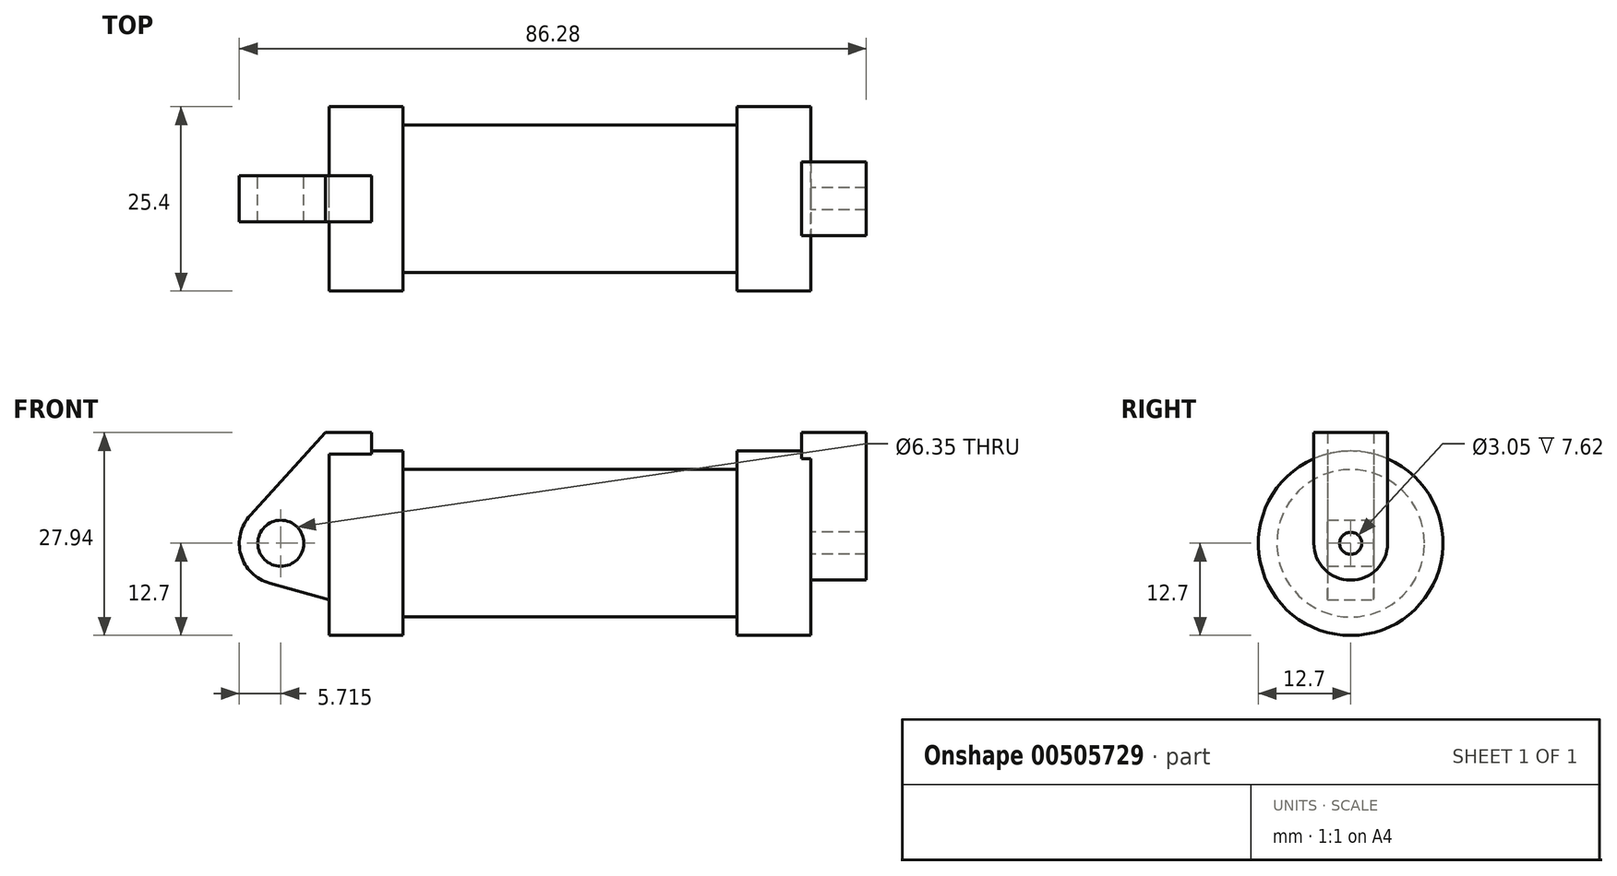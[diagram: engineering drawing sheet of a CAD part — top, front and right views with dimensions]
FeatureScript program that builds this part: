
annotation { "Feature Type Name" : "Feature", "Feature Type Description" : "" }
export const myFeature = defineFeature(function(context is Context, id is Id, definition is map)
    precondition{}
    {
        {
            var Q0;
            Q0=qCreatedBy(makeId("Front.planeOp"),FACE);
            var sketch = newSketch(context, id + "F0", { "sketchPlane" : qUnion([Q0])});
            skLineSegment(sketch, "E0", {"start": v(0, 0) * mm, "end": v(0, 12.7) * mm});
            skLineSegment(sketch, "E1", {"start": v(0, 12.7) * mm, "end": v(10.16, 12.7) * mm});
            skLineSegment(sketch, "E2", {"start": v(10.16, 12.7) * mm, "end": v(10.16, 10.16) * mm});
            skLineSegment(sketch, "E3", {"start": v(10.16, 10.16) * mm, "end": v(56.13, 10.16) * mm});
            skLineSegment(sketch, "E4", {"start": v(56.13, 10.16) * mm, "end": v(56.13, 12.7) * mm});
            skLineSegment(sketch, "E5", {"start": v(56.13, 12.7) * mm, "end": v(66.3, 12.7) * mm});
            skLineSegment(sketch, "E6", {"start": v(66.3, 12.7) * mm, "end": v(66.3, 0) * mm});
            skLineSegment(sketch, "E7", {"start": v(66.3, 0) * mm, "end": v(0, 0) * mm});
            skLineSegment(sketch, "E8", {"start": v(5.84, 15.24) * mm, "end": v(-0.5, 15.24) * mm});
            skLineSegment(sketch, "E9", {"start": v(-0.5, 15.24) * mm, "end": v(-10.88, 3.85) * mm});
            skLineSegment(sketch, "E10", {"start": v(0, 0) * mm, "end": v(-6.65, 0) * mm});
            skCircle(sketch, "E11", {"center": v(-6.65, 0) * mm, "radius": 5.72 * mm});
            skCircle(sketch, "E12", {"center": v(-6.65, 0) * mm, "radius": 3.18 * mm});
            skLineSegment(sketch, "E13", {"start": v(5.84, 15.24) * mm, "end": v(5.84, -9.4) * mm});
            skLineSegment(sketch, "E14", {"start": v(5.84, -9.4) * mm, "end": v(-8.18, -5.5) * mm});
            skSolve(sketch);
        }
        {
            var Q0;
            {var subQ0=sQuery(id+"F0.wireOp",EDGE,"E2");Q0=makeQuery(id+"F0.imprint","IMPRINT",FACE,{"disambiguationData":[TD([[makeQuery(id+"F0.imprint","IMPRINT",EDGE,{"derivedFrom":subQ0}),-1.0]])]});}
            var Q1;
            {var subQ0=sQuery(id+"F0.wireOp",EDGE,"E0");Q1=makeQuery(id+"F0.imprint","IMPRINT",FACE,{"disambiguationData":[TD([[makeQuery(id+"F0.imprint","IMPRINT",EDGE,{"derivedFrom":subQ0}),-1.0]])]});}
            var Q2;
            Q2=sQuery(id+"F0.wireOp",EDGE,"E10");
            revolve(context, id + "F1", {"entities" : qUnion([Q0, Q1]), "axis" : qUnion([Q2]), "revolveType" : RevolveType.FULL});
        }
        {
            var Q0;
            Q0=makeQuery(id+"F1.opRevolve","SWEPT_FACE",FACE,{"disambiguationData":[OSD([sQuery(id+"F0.wireOp",EDGE,"E6")])]});
            var sketch = newSketch(context, id + "F2", { "sketchPlane" : qUnion([Q0])});
            skCircle(sketch, "E15", {"center": v(0, 0) * mm, "radius": 1.52 * mm});
            skCircle(sketch, "E16", {"center": v(0, 0) * mm, "radius": 5.08 * mm});
            skLineSegment(sketch, "E17", {"start": v(-5.08, 0) * mm, "end": v(-5.08, 15.24) * mm});
            skLineSegment(sketch, "E18", {"start": v(0, 0) * mm, "end": v(-15.97, 0) * mm, "construction": true});
            skLineSegment(sketch, "E19", {"start": v(0, 0) * mm, "end": v(15.9, 0) * mm, "construction": true});
            skLineSegment(sketch, "E20", {"start": v(5.08, 0) * mm, "end": v(5.08, 15.24) * mm});
            skLineSegment(sketch, "E21", {"start": v(-5.08, 15.24) * mm, "end": v(5.08, 15.24) * mm});
            skSolve(sketch);
        }
        {
            var Q0;
            Q0 = qSketchRegion(id + "F2", true);
            extrude(context, id + "F3", {"entities" : qUnion([Q0]), "operationType" : NewBodyOperationType.ADD, "depth" : 7.62 * mm, "hasSecondDirection" : true, "secondDirectionOppositeDirection" : true, "secondDirectionDepth" : 1.27 * mm});
        }
        {
            var Q0;
            {var subQ5=sQuery(id+"F0.wireOp",EDGE,"E12");Q0=makeQuery(id+"F0.imprint","IMPRINT",FACE,{"disambiguationData":[TD([[makeQuery(id+"F0.imprint","IMPRINT",EDGE,{"derivedFrom":subQ5}),-1.0]])]});}
            var Q1;
            {var subQ1=sQuery(id+"F0.wireOp",EDGE,"E0");Q1=makeQuery(id+"F0.imprint","IMPRINT",FACE,{"disambiguationData":[TD([[makeQuery(id+"F0.imprint","IMPRINT",EDGE,{"derivedFrom":subQ1}),1.0]])]});}
            var Q2;
            {var subQ0=sQuery(id+"F0.wireOp",EDGE,"E14");Q2=makeQuery(id+"F0.imprint","IMPRINT",FACE,{"disambiguationData":[TD([[makeQuery(id+"F0.imprint","IMPRINT",EDGE,{"derivedFrom":subQ0}),-1.0]])]});}
            var Q3;
            {var subQ0=sQuery(id+"F0.wireOp",EDGE,"E0");Q3=makeQuery(id+"F0.imprint","IMPRINT",FACE,{"disambiguationData":[TD([[makeQuery(id+"F0.imprint","IMPRINT",EDGE,{"derivedFrom":subQ0}),-1.0]])]});}
            extrude(context, id + "F4", {"entities" : qUnion([Q0, Q1, Q2, Q3]), "operationType" : NewBodyOperationType.ADD, "endBound" : BoundingType.SYMMETRIC, "depth" : 6.35 * mm});
        }
    });
